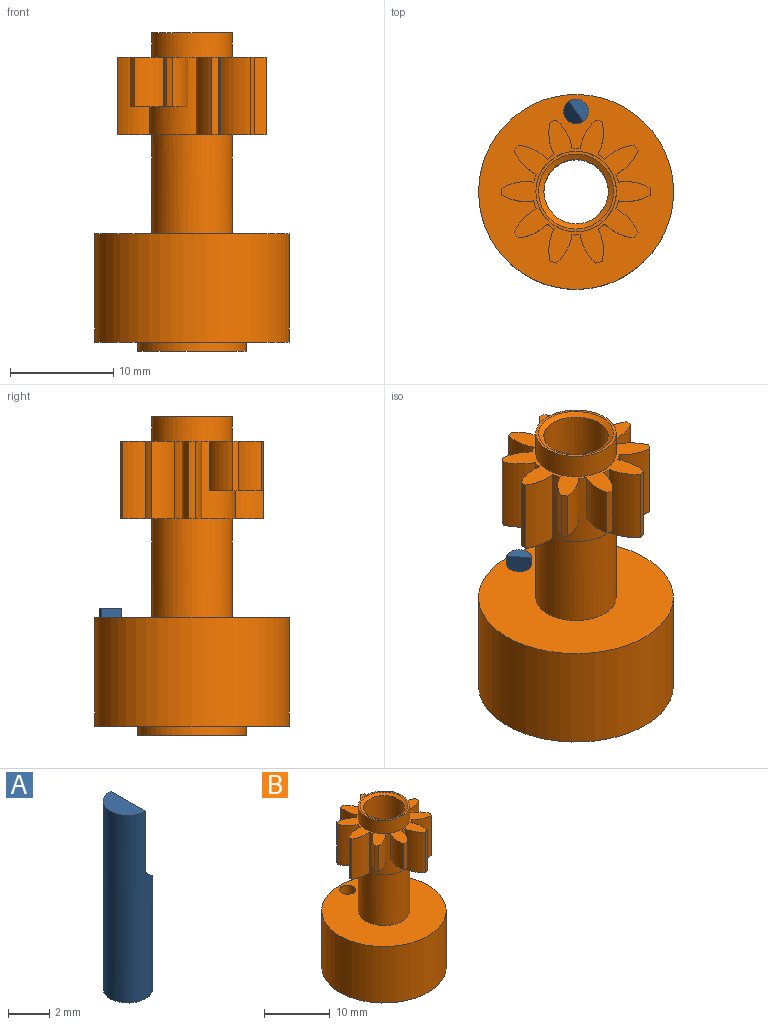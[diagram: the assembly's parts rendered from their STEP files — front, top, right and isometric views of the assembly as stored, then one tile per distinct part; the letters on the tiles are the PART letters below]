
ASSEMBLY  parts=2 mates=1
PART A: 5 faces, bbox 2.4x2.4x11.1 mm
  f0: cylinder r=1.2mm len=11.1mm, axis (0,0,-1), area 67.2mm2, adj f1,f2,f3,f4
  f1: plane 2.4x1.2mm, normal (0,0,1), area 2.3mm2, adj f0,f3
  f2: plane 2.4x2.4mm, normal (0,0,-1), area 4.5mm2, adj f0
  f3: plane 3.6x2.4mm, normal (1,0,0), area 8.6mm2, adj f0,f1,f4
  f4: plane 2.4x1.2mm, normal (0.71,0,0.71), area 3.2mm2, adj f0,f3
PART B: 54 faces, bbox 18.9x18.9x30.9 mm
  f0: plane 14.4x13.88mm, normal (0,0,-1), area 46.7mm2, adj f1,f2,f3,f10,f11,f12,f13,f14
  f1: cylinder r=4.5mm len=7.5mm, axis (0,0,-1), area 24.1mm2, adj f0,f2,f38,f39
  f2: cylinder r=7.2mm len=7.5mm, axis (0,0,-1), area 4.8mm2, adj f0,f1,f3,f39
  f3: cylinder r=4.5mm len=7.5mm, axis (0,0,-1), area 24.1mm2, adj f0,f2,f10,f39
  f4: cylinder r=4.5mm len=4.8mm, axis (0,0,-1), area 15.4mm2, adj f5,f10,f39,f41
  f5: cylinder r=7.2mm len=4.8mm, axis (0,0,-1), area 3.1mm2, adj f4,f6,f39,f41
  f6: cylinder r=4.5mm len=4.8mm, axis (0,0,-1), area 15.4mm2, adj f5,f10,f39,f41
  f7: cylinder r=4.5mm len=4.8mm, axis (0,0,-1), area 15.4mm2, adj f8,f10,f39,f40
  f8: cylinder r=7.2mm len=4.8mm, axis (0,0,-1), area 3.1mm2, adj f7,f9,f39,f40
  f9: cylinder r=4.5mm len=4.8mm, axis (0,0,-1), area 15.4mm2, adj f8,f10,f39,f40
  f10: cylinder r=4.2mm len=7.5mm, axis (0,0,-1), area 28mm2, adj f0,f3,f4,f6,f7,f9,f11,f39
  f11: cylinder r=4.5mm len=7.5mm, axis (0,0,-1), area 24.1mm2, adj f0,f10,f12,f39
  f12: cylinder r=7.2mm len=7.5mm, axis (0,0,-1), area 4.8mm2, adj f0,f11,f13,f39
  f13: cylinder r=4.5mm len=7.5mm, axis (0,0,-1), area 24.1mm2, adj f0,f12,f14,f39
  f14: cylinder r=4.2mm len=7.5mm, axis (0,0,-1), area 6mm2, adj f0,f13,f15,f39
  f15: cylinder r=4.5mm len=7.5mm, axis (0,0,-1), area 24.1mm2, adj f0,f14,f16,f39
  f16: cylinder r=7.2mm len=7.5mm, axis (0,0,-1), area 4.8mm2, adj f0,f15,f17,f39
  f17: cylinder r=4.5mm len=7.5mm, axis (0,0,-1), area 24.1mm2, adj f0,f16,f18,f39
  f18: cylinder r=4.2mm len=7.5mm, axis (0,0,-1), area 6mm2, adj f0,f17,f19,f39
  f19: cylinder r=4.5mm len=7.5mm, axis (0,0,-1), area 24.1mm2, adj f0,f18,f20,f39
  f20: cylinder r=7.2mm len=7.5mm, axis (0,0,-1), area 4.8mm2, adj f0,f19,f21,f39
  f21: cylinder r=4.5mm len=7.5mm, axis (0,0,-1), area 24.1mm2, adj f0,f20,f22,f39
  f22: cylinder r=4.2mm len=7.5mm, axis (0,0,-1), area 6mm2, adj f0,f21,f23,f39
  f23: cylinder r=4.5mm len=7.5mm, axis (0,0,-1), area 24.1mm2, adj f0,f22,f24,f39
  f24: cylinder r=7.2mm len=7.5mm, axis (0,0,-1), area 4.8mm2, adj f0,f23,f25,f39
  f25: cylinder r=4.5mm len=7.5mm, axis (0,0,-1), area 24.1mm2, adj f0,f24,f26,f39
  f26: cylinder r=4.2mm len=7.5mm, axis (0,0,-1), area 6mm2, adj f0,f25,f27,f39
  f27: cylinder r=4.5mm len=7.5mm, axis (0,0,-1), area 24.1mm2, adj f0,f26,f28,f39
  f28: cylinder r=7.2mm len=7.5mm, axis (0,0,-1), area 4.8mm2, adj f0,f27,f29,f39
  f29: cylinder r=4.5mm len=7.5mm, axis (0,0,-1), area 24.1mm2, adj f0,f28,f30,f39
  f30: cylinder r=4.2mm len=7.5mm, axis (0,0,-1), area 6mm2, adj f0,f29,f31,f39
  f31: cylinder r=4.5mm len=7.5mm, axis (0,0,-1), area 24.1mm2, adj f0,f30,f32,f39
  f32: cylinder r=7.2mm len=7.5mm, axis (0,0,-1), area 4.8mm2, adj f0,f31,f33,f39
  f33: cylinder r=4.5mm len=7.5mm, axis (0,0,-1), area 24.1mm2, adj f0,f32,f34,f39
  f34: cylinder r=4.2mm len=7.5mm, axis (0,0,-1), area 6mm2, adj f0,f33,f35,f39
  f35: cylinder r=4.5mm len=7.5mm, axis (0,0,-1), area 24.1mm2, adj f0,f34,f36,f39
  f36: cylinder r=7.2mm len=7.5mm, axis (0,0,-1), area 4.8mm2, adj f0,f35,f37,f39
  f37: cylinder r=4.5mm len=7.5mm, axis (0,0,-1), area 24.1mm2, adj f0,f36,f38,f39
  f38: cylinder r=4.2mm len=7.5mm, axis (0,0,-1), area 6mm2, adj f0,f1,f37,f39
  f39: plane 14.4x13.88mm, normal (0,0,1), area 56.4mm2, adj f1,f2,f3,f4,f5,f6,f7,f8
  f40: plane 3.32x2.24mm, normal (0,0,-1), area 4.9mm2, adj f7,f8,f9,f10
  f41: plane 3.22x2.81mm, normal (0,0,-1), area 4.9mm2, adj f4,f5,f6,f10
  f42: cylinder r=3.9mm len=9.6mm, axis (0,0,-1), area 235.2mm2, adj f0,f48
  f43: cone r=3.12mm half-angle=30deg, axis (0,0,-1), area 49.7mm2, adj f44,f51
  f44: plane 10.5x10.5mm, normal (0,0,-1), area 31.2mm2, adj f43,f45
  f45: cylinder r=5.25mm len=10.5mm, axis (0,0,-1), area 29.7mm2, adj f44,f46
  f46: plane 18.9x18.9mm, normal (0,0,-1), area 189.4mm2, adj f45,f47,f52
  f47: cylinder r=9.45mm len=18.9mm, axis (0,0,-1), area 623.4mm2, adj f46,f48
  f48: plane 18.9x18.9mm, normal (0,0,1), area 228.2mm2, adj f42,f47,f52
  f49: cylinder r=3.9mm len=7.8mm, axis (0,0,-1), area 58.8mm2, adj f39,f50
  f50: plane 7.8x7.8mm, normal (0,0,1), area 6.2mm2, adj f49,f53
  f51: cylinder r=3.12mm len=28.73mm, axis (0,0,-1), area 563.2mm2, adj f43,f53
  f52: cylinder r=1.2mm len=10.5mm, axis (0,0,1), area 79.2mm2, adj f46,f48
  f53: cone r=3.64mm half-angle=60deg, axis (0,0,1), area 12.7mm2, adj f50,f51
PLACE A rot(axis=(0,0,-1),144deg) t=(0,2.6,-6.4)mm
PLACE B t=(0,-5.2,-7.6)mm
MATE fastened A.f0 <-> B.f52  axis (0,0,-1) through (0,2.6,4.7)mm
